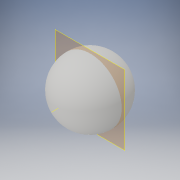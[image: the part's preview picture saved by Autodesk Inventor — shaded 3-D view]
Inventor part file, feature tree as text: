
AUTODESK INVENTOR PART (.ipt)
format: ipt  version: 2019.1 (Build 231200000, 200)  size: 119,296 bytes
history: native  units: in
note: dims shown in document units (in); Inventor stores cm internally (conversion verified against a paired STEP export)
features: revolve x1, sketch x1
ambient origin geometry x8: Origin, YZ Plane, XZ Plane, XY Plane, X Axis, Y Axis, Z Axis, Center Point
bodies: Solid1 (feature_tree)
feature tree (2):
  revolve  "Revolution1"  Angle=180.0deg
  sketch  "Sketch2"  dims[d1=0.45in d2=180.0deg]
